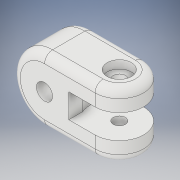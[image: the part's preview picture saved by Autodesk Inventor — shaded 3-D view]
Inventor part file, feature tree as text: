
AUTODESK INVENTOR PART (.ipt)
format: ipt  version: 2017 SP1 (Build 210196100, 196)  size: 193,536 bytes
history: native  units: in
note: dims shown in document units (in); Inventor stores cm internally (conversion verified against a paired STEP export)
features: extrude x5, sketch x5, fillet x1, projected_geometry x1
ambient origin geometry x8: Origin, YZ Plane, XZ Plane, XY Plane, X Axis, Y Axis, Z Axis, Center Point
bodies: Solid1 (feature_tree)
feature tree (12):
  extrude  "Extrusion1"  Depth=0.6299in
  extrude  "Extrusion2"  Depth=0.4724in TaperAngle=0.0deg
  extrude  "Extrusion3"  Depth=0.4724in
  extrude  "Extrusion4"  Depth=0.1969in TaperAngle=0.0deg
  extrude  "Extrusion5"  Depth=0.2362in
  fillet  "Fillet1"  Radius=0.0787in
  sketch  "Sketch2"  dims[d0=0.1575in d1=0.6299in]
  sketch  "Sketch3"  dims[d2=0.2362in d3=0.4724in d4=0.0in]
  sketch  "Sketch4"  dims[d5=0.4724in d6=0.4921in]
  projected_geometry  "Projected Loop1"
  sketch  "Sketch6"  dims[d7=0.1181in d8=0.1969in d9=0.0in]
  sketch  "Sketch7"  dims[d10=0.1969in d11=0.0in d13=0.2362in d14=0.0787in d15=0.0in d16=0.5512in d17=0.2362in d18=0.0in d19=0.0787in]
